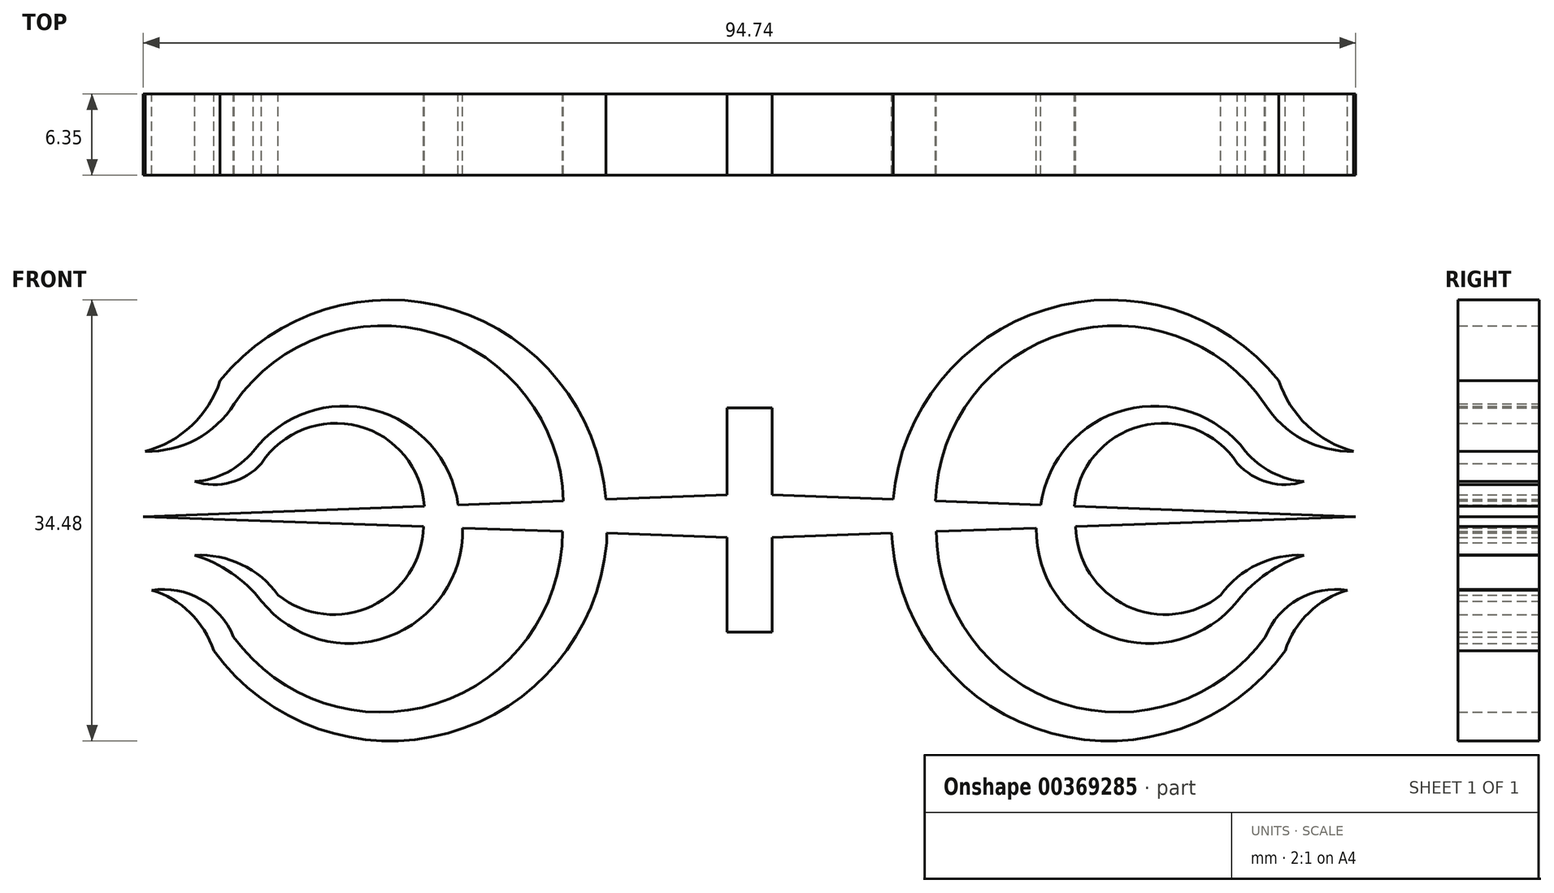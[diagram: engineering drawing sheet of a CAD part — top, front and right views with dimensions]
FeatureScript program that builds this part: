
annotation { "Feature Type Name" : "Feature", "Feature Type Description" : "" }
export const myFeature = defineFeature(function(context is Context, id is Id, definition is map)
    precondition{}
    {
        {
            var Q0;
            Q0=qCreatedBy(makeId("Front.planeOp"),FACE);
            var sketch = newSketch(context, id + "F0", { "sketchPlane" : qUnion([Q0])});
            skArc(sketch, "E0", {"start": v(-14.53, 1.66) * mm, "mid": v(-24.45, 15.14) * mm, "end": v(-40.27, 9.66) * mm});
            skArc(sketch, "E1", {"start": v(-11.19, 1.66) * mm, "mid": v(-22.9, 16.96) * mm, "end": v(-41.37, 11.48) * mm});
            skArc(sketch, "E2", {"start": v(-47.2, 5.96) * mm, "mid": v(-43.24, 6.89) * mm, "end": v(-40.27, 9.66) * mm});
            skArc(sketch, "E3", {"start": v(-47.2, 5.96) * mm, "mid": v(-43.58, 7.97) * mm, "end": v(-41.37, 11.48) * mm});
            skArc(sketch, "E4", {"start": v(-22.75, 1.66) * mm, "mid": v(-29.32, 9.18) * mm, "end": v(-38.77, 5.96) * mm});
            skArc(sketch, "E5", {"start": v(-25.4, 1.66) * mm, "mid": v(-30.56, 7.93) * mm, "end": v(-38.14, 5) * mm});
            skArc(sketch, "E6", {"start": v(-43.34, 3.59) * mm, "mid": v(-40.81, 4.3) * mm, "end": v(-38.77, 5.96) * mm});
            skArc(sketch, "E7", {"start": v(-43.34, 3.59) * mm, "mid": v(-40.53, 3.53) * mm, "end": v(-38.14, 5) * mm});
            skArc(sketch, "E8", {"start": v(-38.14, -5.75) * mm, "mid": v(-28.23, -8.54) * mm, "end": v(-22.41, -0.04) * mm});
            skArc(sketch, "E9", {"start": v(-36.83, -5.3) * mm, "mid": v(-29.5, -6.13) * mm, "end": v(-25.48, 0.06) * mm});
            skArc(sketch, "E10", {"start": v(-36.83, -5.3) * mm, "mid": v(-39.69, -2.9) * mm, "end": v(-43.34, -2.17) * mm});
            skArc(sketch, "E11", {"start": v(-38.14, -5.75) * mm, "mid": v(-40.47, -3.56) * mm, "end": v(-43.34, -2.17) * mm});
            skArc(sketch, "E12", {"start": v(-40.32, -8.55) * mm, "mid": v(-24.47, -13.77) * mm, "end": v(-14.6, -0.32) * mm});
            skArc(sketch, "E13", {"start": v(-40.32, -8.55) * mm, "mid": v(-42.89, -5.6) * mm, "end": v(-46.73, -4.9) * mm});
            skLineSegment(sketch, "E14", {"start": v(-1.76, 2.56) * mm, "end": v(-47.37, 0.83) * mm});
            skLineSegment(sketch, "E15", {"start": v(-47.37, 0.83) * mm, "end": v(-1.76, -0.77) * mm});
            skLineSegment(sketch, "E16", {"start": v(-1.76, -0.77) * mm, "end": v(-47.37, 0.83) * mm});
            skArc(sketch, "E17.MirrorCS", {"start": v(11.19, 1.66) * mm, "mid": v(22.9, 16.96) * mm, "end": v(41.37, 11.48) * mm});
            skArc(sketch, "E18.MirrorCS", {"start": v(14.53, 1.66) * mm, "mid": v(24.45, 15.14) * mm, "end": v(40.27, 9.66) * mm});
            skArc(sketch, "E19.MirrorCS", {"start": v(47.2, 5.96) * mm, "mid": v(43.58, 7.97) * mm, "end": v(41.37, 11.48) * mm});
            skArc(sketch, "E20.MirrorCS", {"start": v(47.2, 5.96) * mm, "mid": v(43.24, 6.89) * mm, "end": v(40.27, 9.66) * mm});
            skArc(sketch, "E21.MirrorCS", {"start": v(22.75, 1.66) * mm, "mid": v(29.32, 9.18) * mm, "end": v(38.77, 5.96) * mm});
            skArc(sketch, "E22.MirrorCS", {"start": v(25.4, 1.66) * mm, "mid": v(30.56, 7.93) * mm, "end": v(38.14, 5) * mm});
            skArc(sketch, "E23.MirrorCS", {"start": v(36.83, -5.3) * mm, "mid": v(29.5, -6.13) * mm, "end": v(25.48, 0.06) * mm});
            skArc(sketch, "E24.MirrorCS", {"start": v(38.14, -5.75) * mm, "mid": v(28.23, -8.54) * mm, "end": v(22.41, -0.04) * mm});
            skArc(sketch, "E25.MirrorCS", {"start": v(43.34, 3.59) * mm, "mid": v(40.53, 3.53) * mm, "end": v(38.14, 5) * mm});
            skArc(sketch, "E26.MirrorCS", {"start": v(43.34, 3.59) * mm, "mid": v(40.81, 4.3) * mm, "end": v(38.77, 5.96) * mm});
            skArc(sketch, "E27.MirrorCS", {"start": v(36.83, -5.3) * mm, "mid": v(39.69, -2.9) * mm, "end": v(43.34, -2.17) * mm});
            skArc(sketch, "E28.MirrorCS", {"start": v(38.14, -5.75) * mm, "mid": v(40.47, -3.56) * mm, "end": v(43.34, -2.17) * mm});
            skArc(sketch, "E29.MirrorCS", {"start": v(40.32, -8.55) * mm, "mid": v(24.47, -13.77) * mm, "end": v(14.6, -0.32) * mm});
            skArc(sketch, "E30.MirrorCS", {"start": v(40.32, -8.55) * mm, "mid": v(42.89, -5.6) * mm, "end": v(46.73, -4.9) * mm});
            skLineSegment(sketch, "E31.MirrorCS", {"start": v(1.76, 2.56) * mm, "end": v(47.37, 0.83) * mm});
            skLineSegment(sketch, "E32.MirrorCS", {"start": v(1.76, -0.77) * mm, "end": v(47.37, 0.83) * mm});
            skLineSegment(sketch, "E33", {"start": v(-1.76, 2.56) * mm, "end": v(-1.76, 9.35) * mm});
            skLineSegment(sketch, "E34", {"start": v(-1.76, 9.35) * mm, "end": v(1.76, 9.35) * mm});
            skLineSegment(sketch, "E35", {"start": v(1.76, 9.35) * mm, "end": v(1.76, 2.56) * mm});
            skLineSegment(sketch, "E36", {"start": v(1.76, -0.77) * mm, "end": v(1.76, -8.16) * mm});
            skLineSegment(sketch, "E37", {"start": v(1.76, -8.16) * mm, "end": v(-1.76, -8.16) * mm});
            skLineSegment(sketch, "E38", {"start": v(-1.76, -8.16) * mm, "end": v(-1.76, -0.77) * mm});
            skArc(sketch, "E39", {"start": v(-41.86, -9.64) * mm, "mid": v(-23.57, -16.08) * mm, "end": v(-11.16, -1.18) * mm});
            skArc(sketch, "E40", {"start": v(-41.86, -9.64) * mm, "mid": v(-43.71, -6.67) * mm, "end": v(-46.73, -4.9) * mm});
            skArc(sketch, "E41.MirrorCS", {"start": v(41.86, -9.64) * mm, "mid": v(23.57, -16.08) * mm, "end": v(11.16, -1.18) * mm});
            skArc(sketch, "E42.MirrorCS", {"start": v(41.86, -9.64) * mm, "mid": v(43.71, -6.67) * mm, "end": v(46.73, -4.9) * mm});
            skLineSegment(sketch, "E43", {"start": v(-11.16, -1.18) * mm, "end": v(-11.16, -0.44) * mm});
            skLineSegment(sketch, "E44", {"start": v(-11.16, -0.44) * mm, "end": v(-11.16, -1.18) * mm});
            skLineSegment(sketch, "E45", {"start": v(11.16, -1.18) * mm, "end": v(11.1, -0.44) * mm});
            skLineSegment(sketch, "E46", {"start": v(11.1, -0.44) * mm, "end": v(11.16, -1.18) * mm});
            skSolve(sketch);
        }
        {
            var Q0;
            Q0 = qSketchRegion(id + "F0", true);
            extrude(context, id + "F1", {"entities" : qUnion([Q0]), "depth" : 6.35 * mm});
        }
    });
